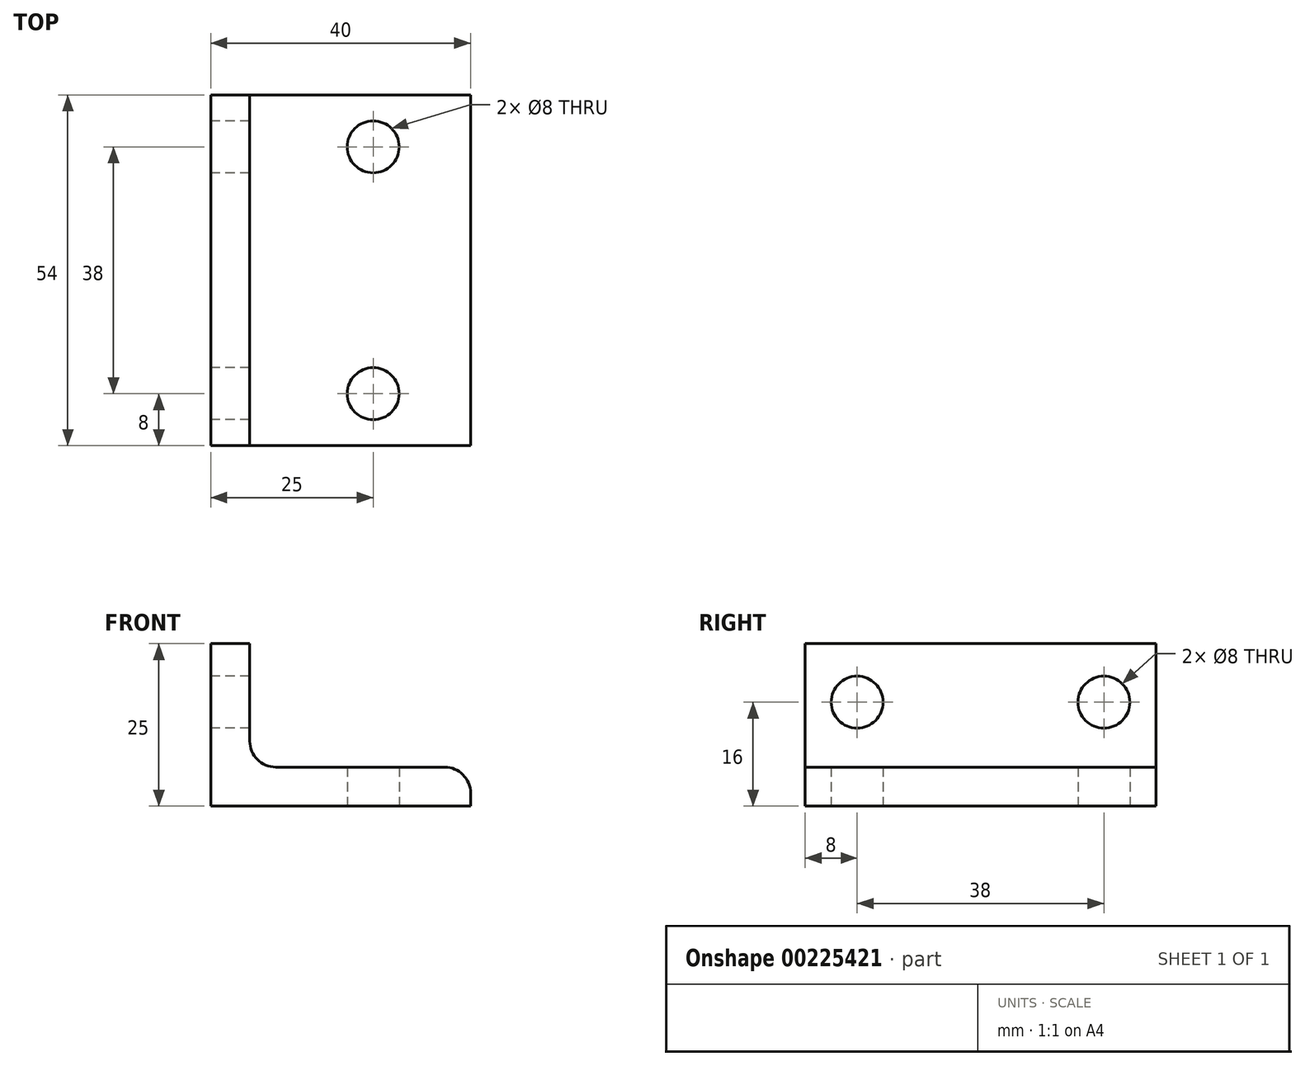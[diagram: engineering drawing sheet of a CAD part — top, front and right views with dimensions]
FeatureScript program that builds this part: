
annotation { "Feature Type Name" : "Feature", "Feature Type Description" : "" }
export const myFeature = defineFeature(function(context is Context, id is Id, definition is map)
    precondition{}
    {
        {
            var Q0;
            Q0=qCreatedBy(makeId("Front.planeOp"),FACE);
            var sketch = newSketch(context, id + "F0", { "sketchPlane" : qUnion([Q0])});
            skLineSegment(sketch, "E0", {"start": v(0, 0) * mm, "end": v(0, 25) * mm});
            skLineSegment(sketch, "E1", {"start": v(0, 25) * mm, "end": v(6, 25) * mm});
            skLineSegment(sketch, "E2", {"start": v(6, 25) * mm, "end": v(6, 6) * mm});
            skLineSegment(sketch, "E3", {"start": v(6, 6) * mm, "end": v(40, 6) * mm});
            skLineSegment(sketch, "E4", {"start": v(40, 6) * mm, "end": v(40, 0) * mm});
            skLineSegment(sketch, "E5", {"start": v(40, 0) * mm, "end": v(0, 0) * mm});
            skSolve(sketch);
        }
        {
            var Q0;
            Q0=makeQuery(id+"F0.imprint","IMPRINT",FACE,{"disambiguationData":[TD([[makeQuery(id+"F0.imprint","IMPRINT",EDGE,{"derivedFrom":sQuery(id+"F0.wireOp",EDGE,"E0")}),-1.0]])]});
            extrude(context, id + "F1", {"entities" : qUnion([Q0]), "depth" : 54 * mm});
        }
        {
            var Q0;
            Q0=makeQuery(id+"F1.opExtrude","SWEPT_EDGE",EDGE,{"disambiguationData":[OSD([sQuery(id+"F0.wireOp",EDGE,"E3"),sQuery(id+"F0.wireOp",EDGE,"E4")])]});
            var Q1;
            Q1=makeQuery(id+"F1.opExtrude","SWEPT_EDGE",EDGE,{"disambiguationData":[OSD([sQuery(id+"F0.wireOp",EDGE,"E2"),sQuery(id+"F0.wireOp",EDGE,"E3")])]});
            fillet(context, id + "F2", {"entities" : qUnion([Q0, Q1]), "radius" : 4 * mm, "tangentPropagation" : true, "allowEdgeOverflow" : false});
        }
        {
            var Q0;
            Q0=makeQuery(id+"F1.opExtrude","SWEPT_FACE",FACE,{"disambiguationData":[OSD([sQuery(id+"F0.wireOp",EDGE,"E0")])]});
            var sketch = newSketch(context, id + "F3", { "sketchPlane" : qUnion([Q0])});
            skPoint(sketch, "E6", {"position": v(8, 16) * mm});
            skPoint(sketch, "E7", {"position": v(46, 16) * mm});
            skSolve(sketch);
        }
        {
            var Q0;
            Q0=sQuery(id+"F3.wireOp",VERTEX,"E6");
            var Q1;
            Q1=sQuery(id+"F3.wireOp",VERTEX,"E7");
            var Q2;
            Q2=makeQuery(id+"F1.opExtrude","SWEPT_BODY",BODY,{"disambiguationData":[OSD([sQuery(id+"F0.wireOp",EDGE,"E0"),sQuery(id+"F0.wireOp",EDGE,"E1"),sQuery(id+"F0.wireOp",EDGE,"E2"),sQuery(id+"F0.wireOp",EDGE,"E3"),sQuery(id+"F0.wireOp",EDGE,"E4"),sQuery(id+"F0.wireOp",EDGE,"E5")])]});
            hole(context, id + "F4", {"style" : HoleStyle.SIMPLE, "endStyle" : HoleEndStyle.BLIND, "holeDiameter" : 8 * mm, "holeDepth" : 25 * mm, "startFromSketch" : true, "locations" : qUnion([Q0, Q1]), "scope" : qUnion([Q2])});
        }
        {
            var Q0;
            Q0=makeQuery(id+"F1.opExtrude","SWEPT_FACE",FACE,{"disambiguationData":[OSD([sQuery(id+"F0.wireOp",EDGE,"E5")])]});
            var sketch = newSketch(context, id + "F5", { "sketchPlane" : qUnion([Q0])});
            skPoint(sketch, "E8", {"position": v(25, 8) * mm});
            skPoint(sketch, "E8.positionSnap0", {"position": v(20, 0) * mm});
            skPoint(sketch, "E9", {"position": v(25, 46) * mm});
            skSolve(sketch);
        }
        {
            var Q0;
            Q0=sQuery(id+"F5.wireOp",VERTEX,"E8");
            var Q1;
            Q1=sQuery(id+"F5.wireOp",VERTEX,"E9");
            var Q2;
            Q2=sQuery(id+"F5.wireOp",VERTEX,"E9");
            var Q3;
            Q3=makeQuery(id+"F1.opExtrude","SWEPT_BODY",BODY,{"disambiguationData":[OSD([sQuery(id+"F0.wireOp",EDGE,"E0"),sQuery(id+"F0.wireOp",EDGE,"E1"),sQuery(id+"F0.wireOp",EDGE,"E2"),sQuery(id+"F0.wireOp",EDGE,"E3"),sQuery(id+"F0.wireOp",EDGE,"E4"),sQuery(id+"F0.wireOp",EDGE,"E5")])]});
            hole(context, id + "F6", {"style" : HoleStyle.SIMPLE, "endStyle" : HoleEndStyle.BLIND, "holeDiameter" : 8 * mm, "holeDepth" : 25 * mm, "startFromSketch" : true, "locations" : qUnion([Q0, Q1, Q2]), "scope" : qUnion([Q3])});
        }
    });
